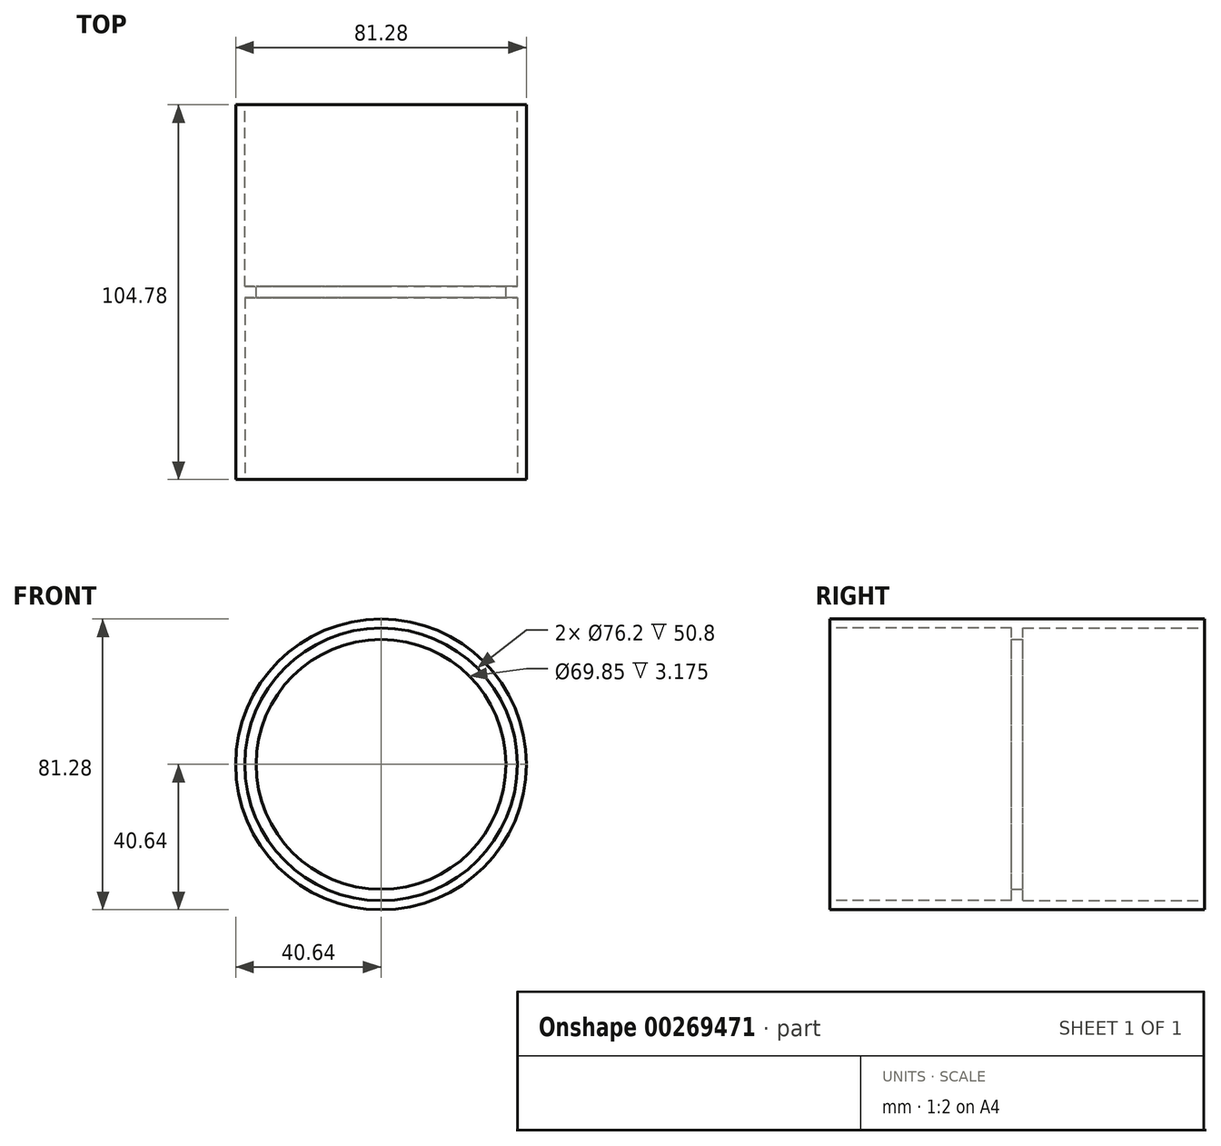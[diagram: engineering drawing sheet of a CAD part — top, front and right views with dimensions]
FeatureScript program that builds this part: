
annotation { "Feature Type Name" : "Feature", "Feature Type Description" : "" }
export const myFeature = defineFeature(function(context is Context, id is Id, definition is map)
    precondition{}
    {
        {
            var Q0;
            Q0=qCreatedBy(makeId("Front.planeOp"),FACE);
            var sketch = newSketch(context, id + "F0", { "sketchPlane" : qUnion([Q0])});
            skCircle(sketch, "E0", {"center": v(0, 0) * mm, "radius": 40.64 * mm});
            skSolve(sketch);
        }
        {
            var Q0;
            Q0 = qSketchRegion(id + "F0", true);
            extrude(context, id + "F1", {"entities" : qUnion([Q0]), "endBound" : BoundingType.SYMMETRIC, "depth" : 3.17 * mm});
        }
        {
            var Q0;
            Q0=qCreatedBy(makeId("Front.planeOp"),FACE);
            var sketch = newSketch(context, id + "F2", { "sketchPlane" : qUnion([Q0])});
            skCircle(sketch, "E1", {"center": v(0, 0) * mm, "radius": 34.93 * mm});
            skSolve(sketch);
        }
        {
            var Q0;
            Q0 = qSketchRegion(id + "F2", true);
            extrude(context, id + "F3", {"entities" : qUnion([Q0]), "operationType" : NewBodyOperationType.REMOVE, "endBound" : BoundingType.THROUGH_ALL, "depth" : 25.4 * mm, "hasSecondDirection" : true, "secondDirectionBound" : SecondDirectionBoundingType.THROUGH_ALL, "secondDirectionOppositeDirection" : true, "secondDirectionDepth" : 25.4 * mm});
        }
        {
            var Q0;
            Q0=makeQuery(id+"F1.opExtrude","CAP_FACE",FACE,{"disambiguationData":[OSD([sQuery(id+"F0.wireOp",EDGE,"E0")])],"isStart":false});
            cPlane(context, id + "F4", {"entities" : qUnion([Q0]), "cplaneType" : CPlaneType.OFFSET, "offset" : 0 * mm, "width" : 152.4 * mm, "height" : 152.4 * mm});
        }
        {
            var Q0;
            Q0=qCreatedBy(id+"F4.planeOp",FACE);
            var sketch = newSketch(context, id + "F5", { "sketchPlane" : qUnion([Q0])});
            skCircle(sketch, "E2", {"center": v(0, 0) * mm, "radius": 40.64 * mm});
            skSolve(sketch);
        }
        {
            var Q0;
            Q0=makeQuery(id+"F5.imprint","IMPRINT",FACE,{"disambiguationData":[TD([[makeQuery(id+"F5.imprint","IMPRINT",EDGE,{"derivedFrom":sQuery(id+"F5.wireOp",EDGE,"E2")}),1.0]])]});
            extrude(context, id + "F6", {"entities" : qUnion([Q0]), "operationType" : NewBodyOperationType.ADD, "depth" : 50.8 * mm});
        }
        {
            var Q0;
            Q0=makeQuery(id+"F6.opExtrude","CAP_FACE",FACE,{"disambiguationData":[OSD([sQuery(id+"F5.wireOp",EDGE,"E2")])],"isStart":false});
            var sketch = newSketch(context, id + "F7", { "sketchPlane" : qUnion([Q0])});
            skCircle(sketch, "E3", {"center": v(0, 0) * mm, "radius": 38.1 * mm});
            skSolve(sketch);
        }
        {
            var Q0;
            Q0=makeQuery(id+"F7.imprint","IMPRINT",FACE,{"disambiguationData":[TD([[makeQuery(id+"F7.imprint","IMPRINT",EDGE,{"derivedFrom":sQuery(id+"F7.wireOp",EDGE,"E3")}),1.0]])]});
            extrude(context, id + "F8", {"entities" : qUnion([Q0]), "operationType" : NewBodyOperationType.REMOVE, "oppositeDirection" : true, "depth" : 50.8 * mm});
        }
        {
            var Q0;
            Q0=makeQuery(id+"F1.opExtrude","SWEPT_BODY",BODY,{"disambiguationData":[OSD([sQuery(id+"F0.wireOp",EDGE,"E0")])]});
            var Q1;
            Q1=qCreatedBy(makeId("Front.planeOp"),FACE);
            mirror(context, id + "F9", {"operationType" : NewBodyOperationType.ADD, "entities" : qUnion([Q0]), "mirrorPlane" : qUnion([Q1])});
        }
    });
